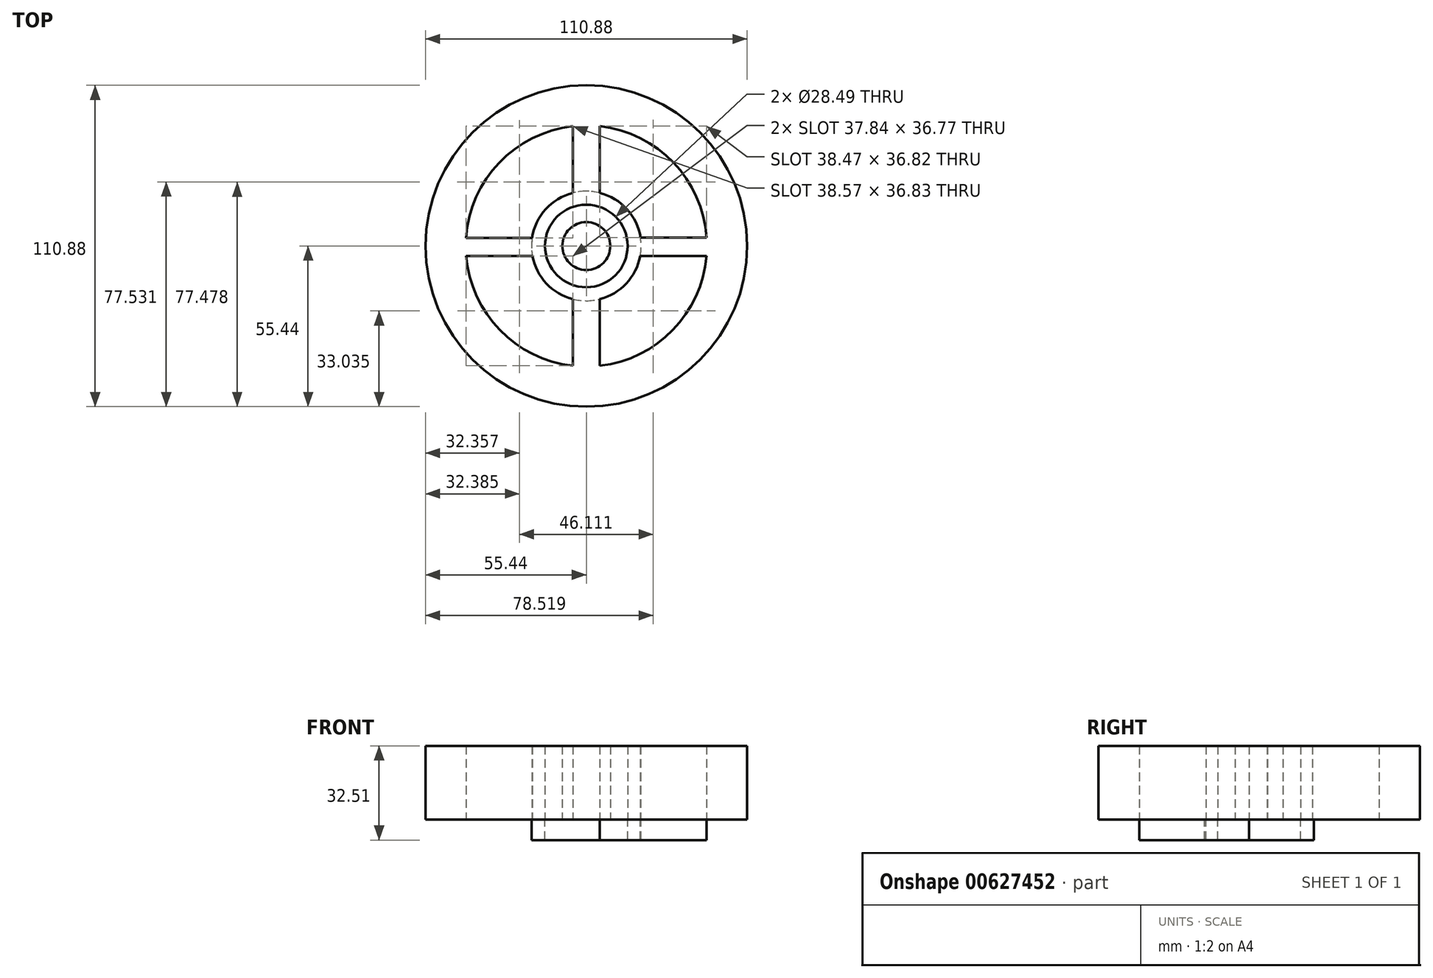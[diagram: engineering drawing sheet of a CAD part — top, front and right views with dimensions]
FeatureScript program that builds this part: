
annotation { "Feature Type Name" : "Feature", "Feature Type Description" : "" }
export const myFeature = defineFeature(function(context is Context, id is Id, definition is map)
    precondition{}
    {
        {
            var Q0;
            Q0=qCreatedBy(makeId("Top.planeOp"),FACE);
            var sketch = newSketch(context, id + "F0", { "sketchPlane" : qUnion([Q0])});
            skCircle(sketch, "E0", {"center": v(0, 0) * mm, "radius": 8.26 * mm});
            skCircle(sketch, "E1", {"center": v(0, 0) * mm, "radius": 14.25 * mm});
            skCircle(sketch, "E2", {"center": v(0, 0) * mm, "radius": 18.9 * mm});
            skCircle(sketch, "E3", {"center": v(0, 0) * mm, "radius": 41.59 * mm});
            skCircle(sketch, "E4", {"center": v(0, 0) * mm, "radius": 55.44 * mm});
            skLineSegment(sketch, "E5", {"start": v(-4.67, -18.3) * mm, "end": v(-4.67, -41.32) * mm});
            skLineSegment(sketch, "E6", {"start": v(4.67, -18.3) * mm, "end": v(4.67, -41.32) * mm});
            skLineSegment(sketch, "E7", {"start": v(-18.57, -3.48) * mm, "end": v(-41.44, -3.48) * mm});
            skLineSegment(sketch, "E8", {"start": v(-18.7, 2.75) * mm, "end": v(-41.5, 2.75) * mm});
            skLineSegment(sketch, "E9", {"start": v(18.68, 2.86) * mm, "end": v(41.49, 2.86) * mm});
            skLineSegment(sketch, "E10", {"start": v(18.57, -3.48) * mm, "end": v(41.44, -3.48) * mm});
            skLineSegment(sketch, "E11", {"start": v(-4.67, 18.3) * mm, "end": v(-4.67, 41.32) * mm});
            skLineSegment(sketch, "E12", {"start": v(4.67, 18.3) * mm, "end": v(4.67, 41.32) * mm});
            skSolve(sketch);
        }
        {
            var Q0;
            Q0=makeQuery(id+"F0.imprint","IMPRINT",FACE,{"disambiguationData":[TD([[makeQuery(id+"F0.imprint","IMPRINT",EDGE,{"derivedFrom":sQuery(id+"F0.wireOp",EDGE,"E4")}),1.0]])]});
            var Q1;
            {var subQ0=sQuery(id+"F0.wireOp",EDGE,"Us6H1OcY-aDeH-QdWZ-2WPP-Vf3EuN3I0Olx");var subQ1=sQuery(id+"F0.wireOp",EDGE,"E1");var subQ2=makeQuery(id+"F0.imprint","INTERSECT",VERTEX,{"disambiguationData":[OD(0.0)],"derivedFrom":[subQ1,subQ0]});Q1=makeQuery(id+"F0.imprint","IMPRINT",FACE,{"disambiguationData":[TD([[makeQuery(id+"F0.imprint","IMPRINT",EDGE,{"disambiguationData":[TD([[subQ2,-1.0]])],"derivedFrom":subQ1}),-1.0]])]});}
            var Q2;
            {var subQ0=sQuery(id+"F0.wireOp",EDGE,"Us6H1OcY-aDeH-QdWZ-2WPP-Vf3EuN3I0Olx");var subQ4=sQuery(id+"F0.wireOp",EDGE,"E1");var subQ5=makeQuery(id+"F0.imprint","INTERSECT",VERTEX,{"disambiguationData":[OD(0.0)],"derivedFrom":[subQ4,subQ0]});Q2=makeQuery(id+"F0.imprint","IMPRINT",FACE,{"disambiguationData":[TD([[makeQuery(id+"F0.imprint","IMPRINT",EDGE,{"disambiguationData":[TD([[subQ5,1.0]])],"derivedFrom":subQ4}),-1.0]])]});}
            var Q3;
            Q3=sQuery(id+"F0.wireOp",EDGE,"PGMmY1YM-dWMW-vSE5-LpKM-V7puUiMCtkwD");
            extrude(context, id + "F1", {"entities" : qUnion([Q0, Q1, Q2]), "surfaceEntities" : qUnion([Q3]), "depth" : 25.4 * mm, "offsetDistance" : 25.4 * mm});
        }
        {
            var Q0;
            Q0 = qSketchRegion(id + "F0", true);
            var Q1;
            {var subQ0=sQuery(id+"F0.wireOp",EDGE,"E11");Q1=makeQuery(id+"F0.imprint","IMPRINT",FACE,{"disambiguationData":[TD([[makeQuery(id+"F0.imprint","IMPRINT",EDGE,{"derivedFrom":subQ0}),-1.0]])]});}
            var Q2;
            {var subQ0=sQuery(id+"F0.wireOp",EDGE,"E7");Q2=makeQuery(id+"F0.imprint","IMPRINT",FACE,{"disambiguationData":[TD([[makeQuery(id+"F0.imprint","IMPRINT",EDGE,{"derivedFrom":subQ0}),-1.0]])]});}
            var Q3;
            {var subQ0=sQuery(id+"F0.wireOp",EDGE,"E5");Q3=makeQuery(id+"F0.imprint","IMPRINT",FACE,{"disambiguationData":[TD([[makeQuery(id+"F0.imprint","IMPRINT",EDGE,{"derivedFrom":subQ0}),1.0]])]});}
            var Q4;
            {var subQ0=sQuery(id+"F0.wireOp",EDGE,"E9");Q4=makeQuery(id+"F0.imprint","IMPRINT",FACE,{"disambiguationData":[TD([[makeQuery(id+"F0.imprint","IMPRINT",EDGE,{"derivedFrom":subQ0}),-1.0]])]});}
            extrude(context, id + "F2", {"entities" : qUnion([Q0, Q1, Q2, Q3, Q4]), "operationType" : NewBodyOperationType.ADD, "depth" : 25.4 * mm, "offsetDistance" : 25.4 * mm});
        }
        {
            var Q0;
            {var subQ0=sQuery(id+"F0.wireOp",EDGE,"E6");Q0=makeQuery(id+"F0.imprint","IMPRINT",FACE,{"disambiguationData":[TD([[makeQuery(id+"F0.imprint","IMPRINT",EDGE,{"derivedFrom":subQ0}),1.0]])]});}
            var Q1;
            Q1=makeQuery(id+"F0.imprint","IMPRINT",FACE,{"disambiguationData":[TD([[makeQuery(id+"F0.imprint","IMPRINT",EDGE,{"derivedFrom":sQuery(id+"F0.wireOp",EDGE,"E1")}),-1.0]])]});
            extrude(context, id + "F3", {"entities" : qUnion([Q0, Q1]), "oppositeDirection" : true, "depth" : 7.11 * mm, "offsetDistance" : 25.4 * mm});
        }
        {
            var Q0;
            Q0=makeQuery(id+"F0.imprint","IMPRINT",FACE,{"disambiguationData":[TD([[makeQuery(id+"F0.imprint","IMPRINT",EDGE,{"derivedFrom":sQuery(id+"F0.wireOp",EDGE,"E0")}),1.0]])]});
            extrude(context, id + "F4", {"entities" : qUnion([Q0]), "depth" : 25.4 * mm, "offsetDistance" : 25.4 * mm});
        }
    });
